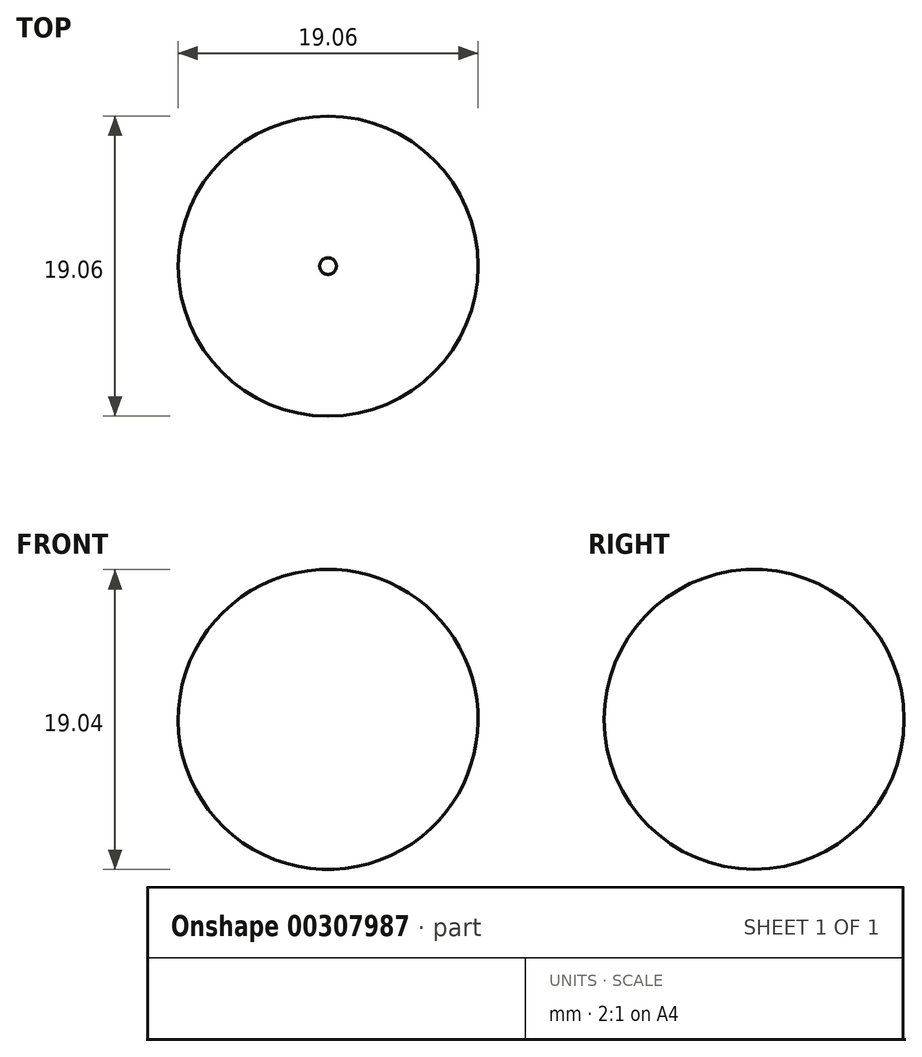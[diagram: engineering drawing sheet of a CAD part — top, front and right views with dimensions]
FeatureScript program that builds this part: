
annotation { "Feature Type Name" : "Feature", "Feature Type Description" : "" }
export const myFeature = defineFeature(function(context is Context, id is Id, definition is map)
    precondition{}
    {
        {
            var Q0;
            Q0=qCreatedBy(makeId("Front.planeOp"),FACE);
            var sketch = newSketch(context, id + "F0", { "sketchPlane" : qUnion([Q0])});
            skCircle(sketch, "E0", {"center": v(0, 0) * mm, "radius": 9.53 * mm});
            skSolve(sketch);
        }
        {
            var Q0;
            Q0=qCreatedBy(makeId("Top.planeOp"),FACE);
            var sketch = newSketch(context, id + "F1", { "sketchPlane" : qUnion([Q0])});
            skArc(sketch, "E1", {"start": v(0, 9.53) * mm, "mid": v(-9.53, 0) * mm, "end": v(0, -9.53) * mm});
            skLineSegment(sketch, "E2", {"start": v(0, 9.53) * mm, "end": v(0, -9.53) * mm});
            skSolve(sketch);
        }
        {
            var Q0;
            Q0 = qSketchRegion(id + "F1", true);
            var Q1;
            Q1=sQuery(id+"F0.wireOp",EDGE,"E0");
            revolve(context, id + "F2", {"entities" : qUnion([Q0]), "axis" : qUnion([Q1]), "revolveType" : RevolveType.FULL});
        }
        {
            var Q0;
            Q0=qCreatedBy(makeId("Top.planeOp"),FACE);
            cPlane(context, id + "F3", {"entities" : qUnion([Q0]), "cplaneType" : CPlaneType.OFFSET, "offset" : 9.52 * mm, "width" : 152.4 * mm, "height" : 152.4 * mm});
        }
        {
            var Q0;
            Q0=qCreatedBy(id+"F3.planeOp",FACE);
            var sketch = newSketch(context, id + "F4", { "sketchPlane" : qUnion([Q0])});
            skCircle(sketch, "E3", {"center": v(0, 0) * mm, "radius": 3.18 * mm});
            skSolve(sketch);
        }
        {
            var Q0;
            Q0 = qSketchRegion(id + "F4", true);
            extrude(context, id + "F5", {"entities" : qUnion([Q0]), "operationType" : NewBodyOperationType.REMOVE, "oppositeDirection" : true, "depth" : 3 / 203.2 * mm});
        }
    });
